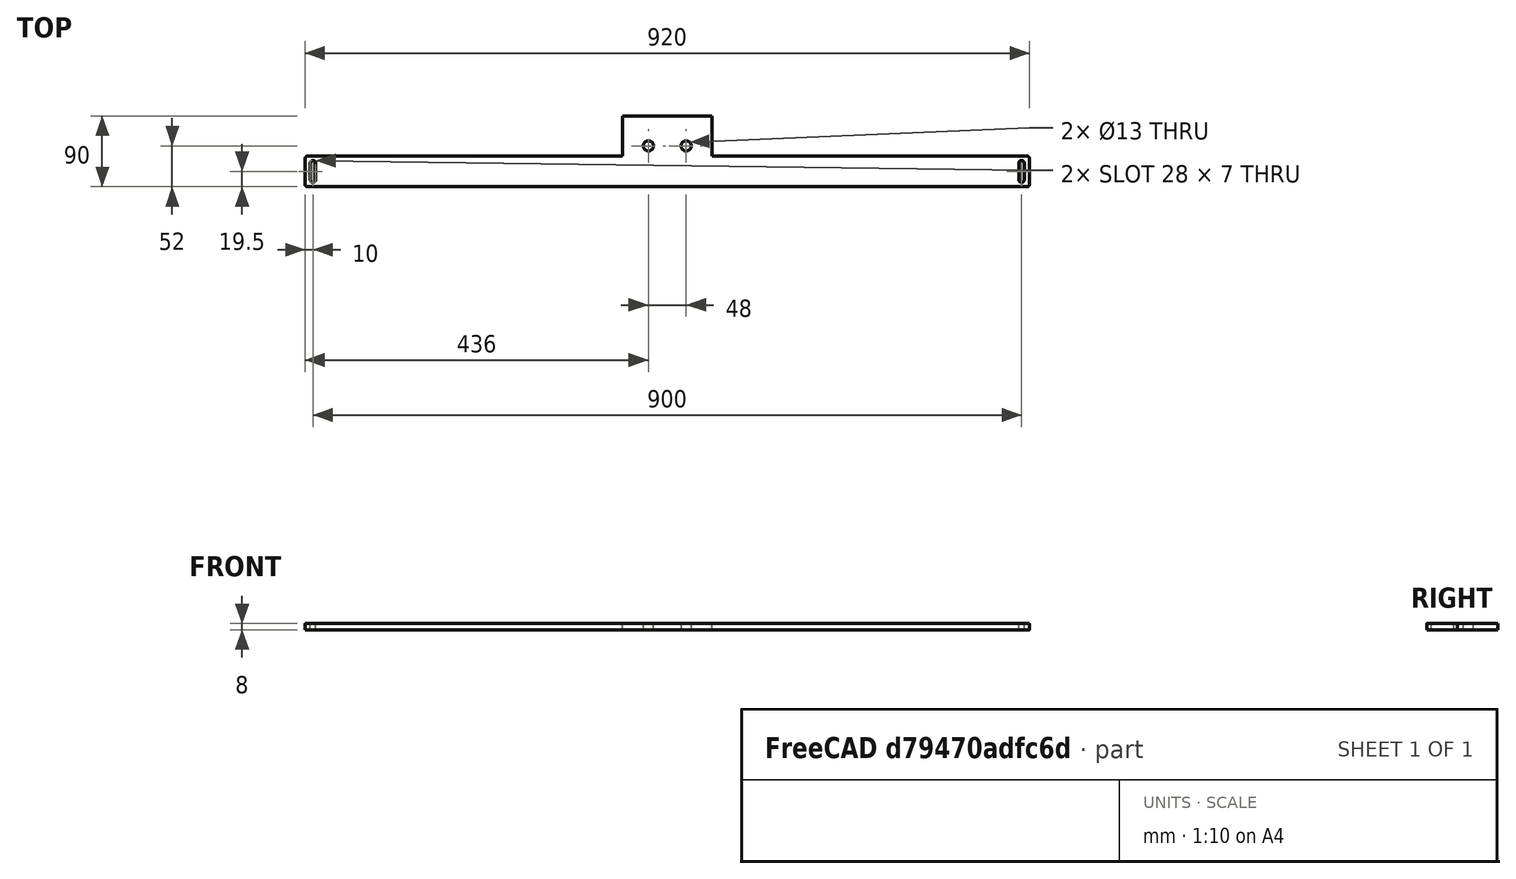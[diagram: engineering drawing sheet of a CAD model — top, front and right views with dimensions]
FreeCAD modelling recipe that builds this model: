
FCSTD DOCUMENT  (FreeCAD 0.19R24366 (Git))
Label: Left right feet plate
License: All rights reserved
LicenseURL: http://en.wikipedia.org/wiki/All_rights_reserved
objects: Sketcher::SketchObject×1, PartDesign::Pad×1, PartDesign::Body×1
note: 4 computed .brp shape members not serialized (recipe doc carries the construction recipe); baked Part::Feature solids carry a one-line shape summary decoded from their .brp

FEATURE [Sketcher::SketchObject] Sketch
  FullyConstrained = true
  MapMode = 5
  Support = -> [XY_Plane]
  sketch-geometry (27):
    g0: Circle CenterX=-24 CenterY=12 CenterZ=0 NormalX=0 NormalY=0 NormalZ=1 AngleXU=0 Radius=6.5
    g1: Circle CenterX=24 CenterY=12 CenterZ=0 NormalX=0 NormalY=0 NormalZ=1 AngleXU=0 Radius=6.5
    g2: LineSegment StartX=-24 StartY=12 StartZ=0 EndX=24 EndY=12 EndZ=0
    g3: LineSegment StartX=-457 StartY=-40 StartZ=0 EndX=0 EndY=-40 EndZ=0
    g4: LineSegment StartX=-460 StartY=-37 StartZ=0 EndX=-460 EndY=-4 EndZ=0
    g5: LineSegment StartX=460 StartY=-37 StartZ=0 EndX=460 EndY=-4 EndZ=0
    g6: ArcOfCircle CenterX=-457 CenterY=-37 CenterZ=0 NormalX=0 NormalY=0 NormalZ=1 AngleXU=0 Radius=3 StartAngle=3.14159 EndAngle=4.71239
    g7: ArcOfCircle CenterX=457 CenterY=-37 CenterZ=0 NormalX=0 NormalY=0 NormalZ=1 AngleXU=0 Radius=3 StartAngle=4.71239 EndAngle=6.28319
    g8: LineSegment StartX=-57 StartY=50 StartZ=0 EndX=57 EndY=50 EndZ=0
    g9: ArcOfCircle CenterX=-457 CenterY=-4 CenterZ=0 NormalX=0 NormalY=0 NormalZ=1 AngleXU=0 Radius=3 StartAngle=1.5708 EndAngle=3.14159
    g10: ArcOfCircle CenterX=457 CenterY=-4 CenterZ=0 NormalX=0 NormalY=0 NormalZ=1 AngleXU=0 Radius=3 StartAngle=0 EndAngle=1.5708
    g11: LineSegment StartX=0 StartY=-40 StartZ=0 EndX=457 EndY=-40 EndZ=0
    g12: ArcOfCircle CenterX=-450 CenterY=-31 CenterZ=0 NormalX=0 NormalY=0 NormalZ=1 AngleXU=0 Radius=3.5 StartAngle=3.14159 EndAngle=6.28319
    g13: ArcOfCircle CenterX=-450 CenterY=-10 CenterZ=0 NormalX=0 NormalY=0 NormalZ=1 AngleXU=0 Radius=3.5 StartAngle=1e-16 EndAngle=3.14159
    g14: LineSegment StartX=-446.5 StartY=-31 StartZ=0 EndX=-446.5 EndY=-10 EndZ=0
    g15: LineSegment StartX=-453.5 StartY=-31 StartZ=0 EndX=-453.5 EndY=-10 EndZ=0
    g16: ArcOfCircle CenterX=450 CenterY=-31 CenterZ=0 NormalX=0 NormalY=0 NormalZ=1 AngleXU=0 Radius=3.5 StartAngle=3.14159 EndAngle=6.28319
    g17: ArcOfCircle CenterX=450 CenterY=-10 CenterZ=0 NormalX=0 NormalY=0 NormalZ=1 AngleXU=0 Radius=3.5 StartAngle=2e-16 EndAngle=3.14159
    g18: LineSegment StartX=453.5 StartY=-31 StartZ=0 EndX=453.5 EndY=-10 EndZ=0
    g19: LineSegment StartX=446.5 StartY=-31 StartZ=0 EndX=446.5 EndY=-10 EndZ=0
    g20: GeomPoint X=0 Y=12 Z=0
    g21: LineSegment StartX=-57 StartY=-1 StartZ=0 EndX=-57 EndY=50 EndZ=0
    g22: LineSegment StartX=57 StartY=50 StartZ=0 EndX=57 EndY=-1 EndZ=0
    g23: LineSegment StartX=-57 StartY=-1 StartZ=0 EndX=-58 EndY=-1 EndZ=0
    g24: LineSegment StartX=-58 StartY=-1 StartZ=0 EndX=-457 EndY=-1 EndZ=0
    g25: LineSegment StartX=57 StartY=-1 StartZ=0 EndX=58 EndY=-1 EndZ=0
    g26: LineSegment StartX=58 StartY=-1 StartZ=0 EndX=457 EndY=-1 EndZ=0
  constraints (63):
    c: Coincident(g2,g0)
    c: Coincident(g2,g1)
    c: Symmetric(g0,g1,g-2)
    c: Equal(g1,g0)
    c: Radius(g1) = 6.5
    c: DistanceX(g2,g2) = 48
    c: Vertical(g4)
    c: Vertical(g5)
    c: Tangent(g4,g6) = 1.5708
    c: Tangent(g3,g6) = -1.5708
    c: Tangent(g5,g7) = -1.5708
    c: Tangent(g4,g9) = 1.5708
    c: Tangent(g5,g10) = -1.5708
    c: Symmetric(g8,g8,g-2)
    c: Symmetric(g3,g11,g-2)
    c: Equal(g9,g6)
    c: Equal(g6,g10)
    c: Radius(g6) = 3
    c: DistanceY(g3,g-1) = 40
    c: Tangent(g12,g15) = 1.5708
    c: Tangent(g12,g14) = -1.5708
    c: Tangent(g14,g13) = -1.5708
    c: Tangent(g15,g13) = 1.5708
    c: Vertical(g14)
    c: Equal(g12,g13)
    c: Radius(g13) = 3.5
    c: DistanceY(g3,g12) = 9
    c: DistanceX(g4,g12) = 10
    c: Tangent(g11,g7) = -1.5708
    c: Symmetric(g4,g5,g-2)
    c: Tangent(g16,g19) = 1.5708
    c: Tangent(g16,g18) = -1.5708
    c: Tangent(g18,g17) = -1.5708
    c: Tangent(g19,g17) = 1.5708
    c: Vertical(g18)
    c: Equal(g17,g13)
    c: Symmetric(g12,g16,g-2)
    c: Symmetric(g13,g17,g-2)
    c: DistanceY(g-1,g8) = 50
    c: PointOnObject(g20,g2)
    c: PointOnObject(g20,g-2)
    c: DistanceY(g-1,g1) = 12
    c: Coincident(g11,g3)
    c: PointOnObject(g3,g-2)
    c: Symmetric(g22,g21,g-2)
    c: DistanceX(g12,g3) = 450
    c: Coincident(g21,g8)
    c: Coincident(g22,g8)
    c: Vertical(g21)
    c: Horizontal(g3)
    c: DistanceX(g8,g8) = 114
    c: Coincident(g23,g21)
    c: Horizontal(g23)
    c: Coincident(g24,g23)
    c: Horizontal(g24)
    c: Coincident(g25,g22)
    c: Coincident(g26,g25)
    c: Symmetric(g25,g23,g-2)
    c: DistanceX(g23,g25) = 116
    c: Tangent(g26,g10) = 1.5708
    c: Tangent(g24,g9) = -1.5708
    c: DistanceY(g3,g9) = 39
    c: DistanceY(g13,g9) = 9
FEATURE [PartDesign::Pad] Pad  label="Plate thickness pad"
  Direction = (1,1,1)
  Length = 8
  Length2 = 100
  Profile = -> Sketch
  Type = 0
FEATURE [PartDesign::Body] Body
  Group = -> [Sketch,Pad]
  Origin = -> Origin
  Tip = -> Pad
